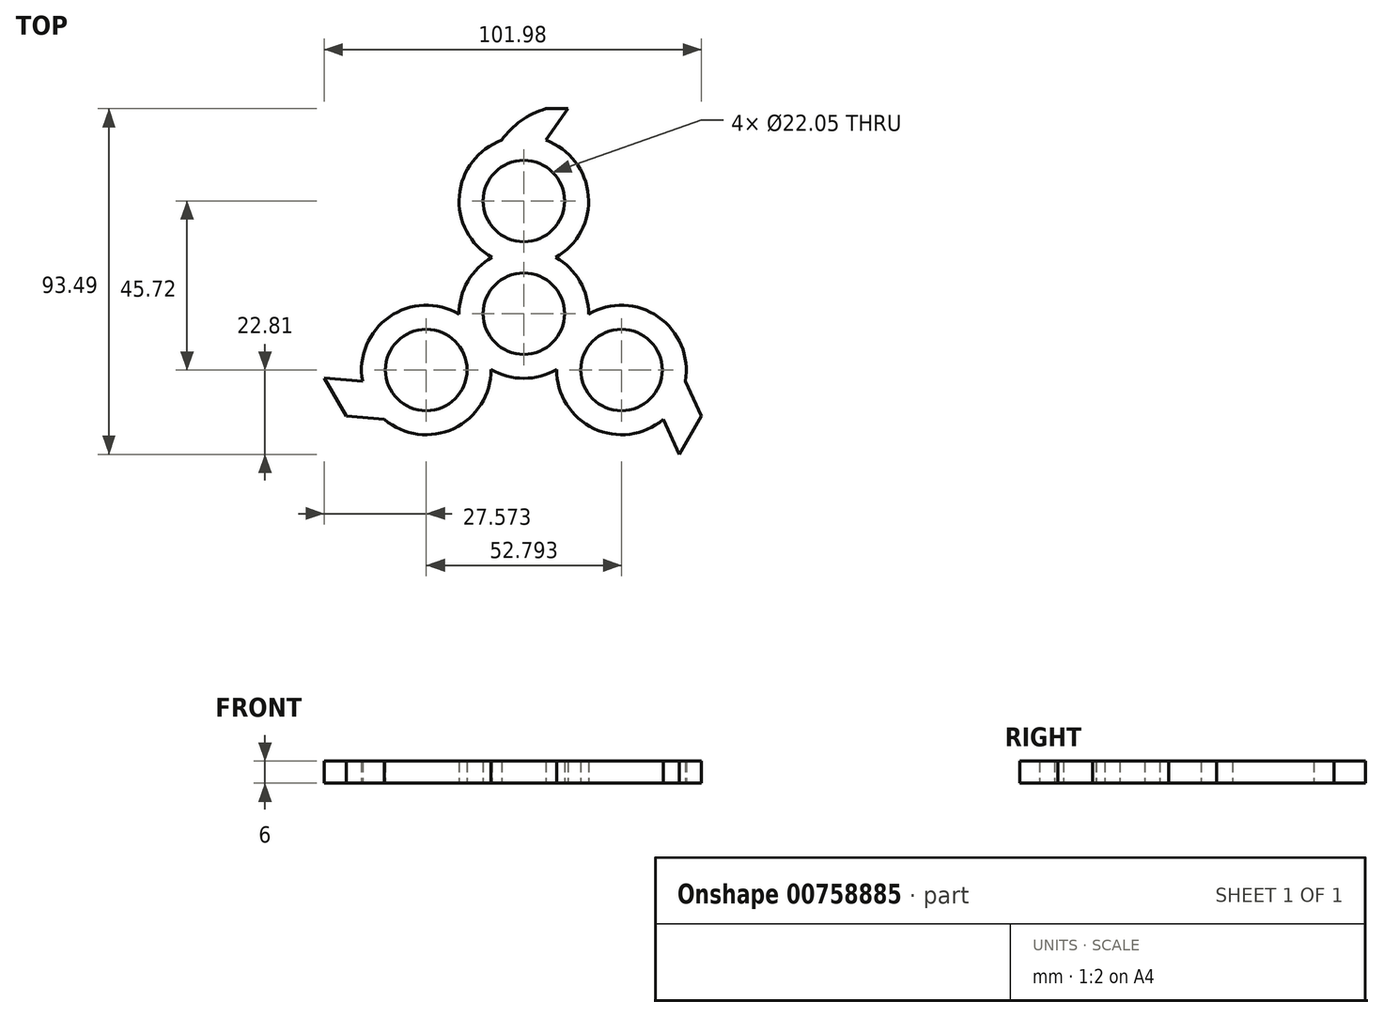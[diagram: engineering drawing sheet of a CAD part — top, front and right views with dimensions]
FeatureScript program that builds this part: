
annotation { "Feature Type Name" : "Feature", "Feature Type Description" : "" }
export const myFeature = defineFeature(function(context is Context, id is Id, definition is map)
    precondition{}
    {
        {
            var Q0;
            Q0=qCreatedBy(makeId("Top.planeOp"),FACE);
            var sketch = newSketch(context, id + "F0", { "sketchPlane" : qUnion([Q0])});
            skCircle(sketch, "E0", {"center": v(0, 30.48) * mm, "radius": 11.03 * mm});
            skCircle(sketch, "E1", {"center": v(0, 0) * mm, "radius": 11.03 * mm});
            skArc(sketch, "E2", {"start": v(8.6, 15.24) * mm, "mid": v(17.44, 31.93) * mm, "end": v(5.96, 46.93) * mm});
            skArc(sketch, "E3", {"start": v(-8.9, -15.07) * mm, "mid": v(0, -17.5) * mm, "end": v(8.9, -15.07) * mm});
            skArc(sketch, "E4.1.0", {"start": v(-17.5, -0.17) * mm, "mid": v(-36.37, -0.86) * mm, "end": v(-43.63, -18.3) * mm});
            skCircle(sketch, "E4.1.1", {"center": v(-26.4, -15.24) * mm, "radius": 11.03 * mm});
            skArc(sketch, "E4.2.0", {"start": v(8.9, -15.07) * mm, "mid": v(18.93, -31.07) * mm, "end": v(37.66, -28.63) * mm});
            skCircle(sketch, "E4.2.1", {"center": v(26.4, -15.24) * mm, "radius": 11.03 * mm});
            skArc(sketch, "E5.trimOffspring", {"start": v(17.5, -0.17) * mm, "mid": v(15.16, 8.75) * mm, "end": v(8.6, 15.24) * mm});
            skArc(sketch, "E6.trimOffspring", {"start": v(-8.6, 15.24) * mm, "mid": v(-15.16, 8.75) * mm, "end": v(-17.5, -0.17) * mm});
            skLineSegment(sketch, "E7", {"start": v(0, 30.48) * mm, "end": v(-17.5, 30.48) * mm, "construction": true});
            skLineSegment(sketch, "E8", {"start": v(-5.96, 46.93) * mm, "end": v(0, 55.44) * mm});
            skArc(sketch, "E9.trimOffspring", {"start": v(-5.96, 46.93) * mm, "mid": v(-17.44, 31.93) * mm, "end": v(-8.6, 15.24) * mm});
            skPoint(sketch, "E10.end.orphan", {"position": v(17.5, 30.48) * mm});
            skLineSegment(sketch, "E11", {"start": v(5.96, 46.93) * mm, "end": v(11.92, 55.44) * mm});
            skLineSegment(sketch, "E12", {"start": v(11.92, 55.44) * mm, "end": v(0, 55.44) * mm});
            skLineSegment(sketch, "E13.1.0", {"start": v(-37.66, -28.63) * mm, "end": v(-48, -27.72) * mm});
            skLineSegment(sketch, "E13.1.1", {"start": v(-53.97, -17.4) * mm, "end": v(-48, -27.72) * mm});
            skLineSegment(sketch, "E13.1.2", {"start": v(-43.63, -18.3) * mm, "end": v(-53.97, -17.4) * mm});
            skLineSegment(sketch, "E13.2.0", {"start": v(43.63, -18.3) * mm, "end": v(48, -27.72) * mm});
            skLineSegment(sketch, "E13.2.1", {"start": v(42.05, -38.05) * mm, "end": v(48, -27.72) * mm});
            skLineSegment(sketch, "E13.2.2", {"start": v(37.66, -28.63) * mm, "end": v(42.05, -38.05) * mm});
            skArc(sketch, "E14.trimOffspring", {"start": v(-37.66, -28.63) * mm, "mid": v(-18.93, -31.07) * mm, "end": v(-8.9, -15.07) * mm});
            skArc(sketch, "E15.trimOffspring", {"start": v(43.63, -18.3) * mm, "mid": v(36.37, -0.86) * mm, "end": v(17.5, -0.17) * mm});
            skArc(sketch, "E16", {"start": v(30.12, 46.93) * mm, "mid": v(12.08, 56.32) * mm, "end": v(-5.96, 46.93) * mm});
            skLineSegment(sketch, "E17", {"start": v(30.12, 46.93) * mm, "end": v(14.08, 40.87) * mm});
            skSolve(sketch);
        }
        {
            var Q0;
            Q0=makeQuery(id+"F0.imprint","IMPRINT",FACE,{"disambiguationData":[TD([[makeQuery(id+"F0.imprint","IMPRINT",EDGE,{"derivedFrom":sQuery(id+"F0.wireOp",EDGE,"E0")}),-1.0]])]});
            extrude(context, id + "F1", {"entities" : qUnion([Q0]), "depth" : 6 * mm, "offsetDistance" : 25.4 * mm});
        }
    });
